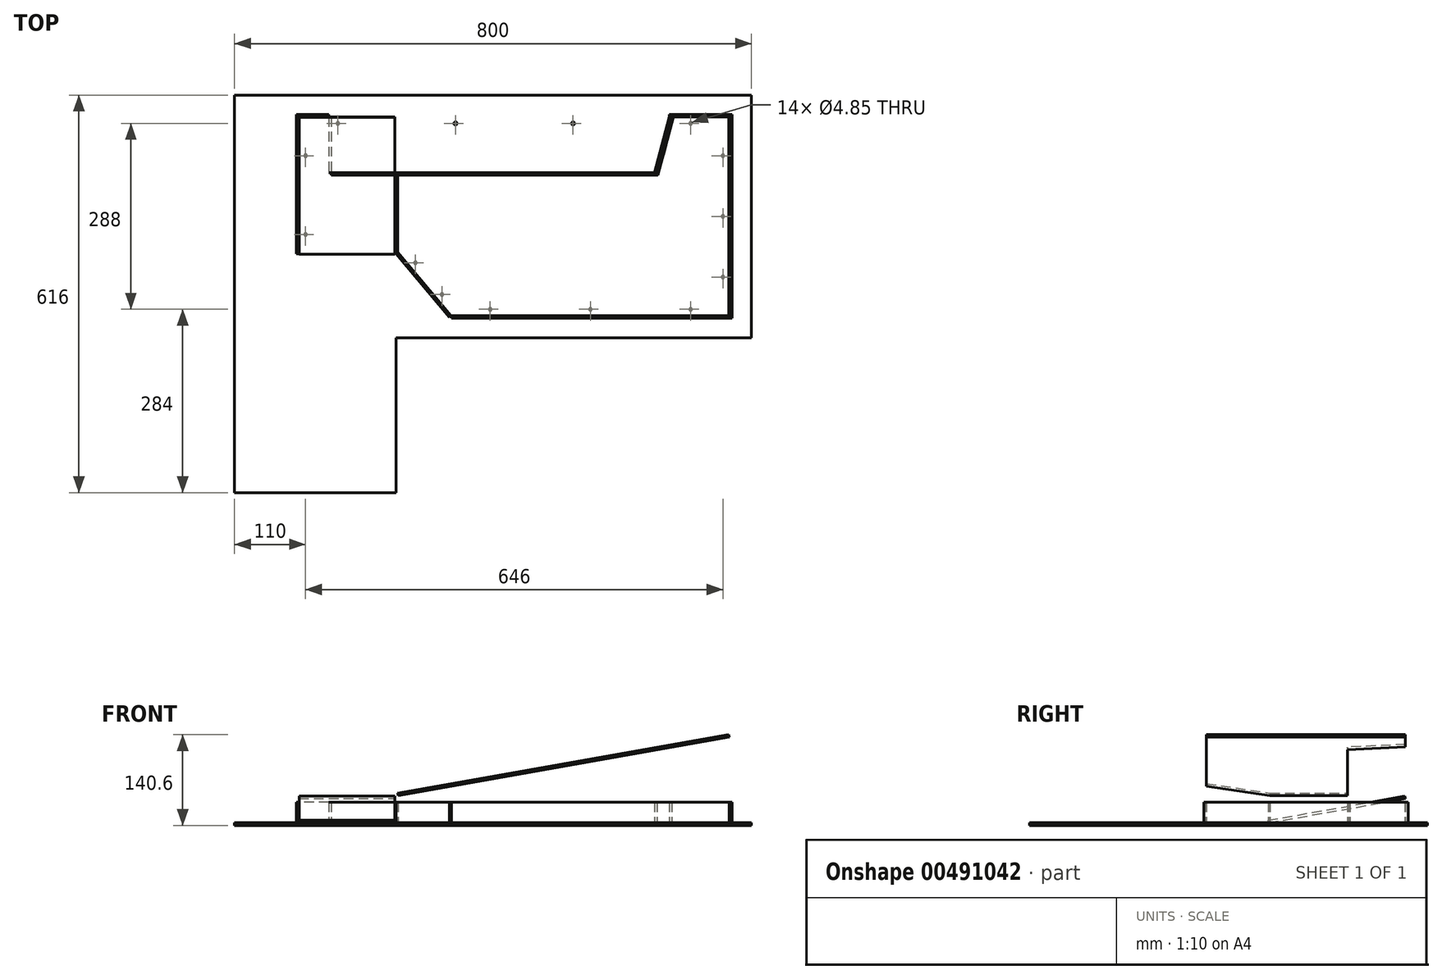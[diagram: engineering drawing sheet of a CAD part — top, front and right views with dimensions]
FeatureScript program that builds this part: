
annotation { "Feature Type Name" : "Feature", "Feature Type Description" : "" }
export const myFeature = defineFeature(function(context is Context, id is Id, definition is map)
    precondition{}
    {
        {
            assignVariable(context, id + "F0", {"name" : "altura", "anyValue" : 32});
        }
        {
            assignVariable(context, id + "F1", {"name" : "inclinacion", "anyValue" : 10});
        }
        {
            var Q0;
            Q0=qCreatedBy(makeId("Top.planeOp"),FACE);
            var sketch = newSketch(context, id + "F2", { "sketchPlane" : qUnion([Q0])});
            skLineSegment(sketch, "E0.bottom", {"start": v(0, 0) * mm, "end": v(250, 0) * mm});
            skLineSegment(sketch, "E0.top", {"start": v(0, 616) * mm, "end": v(800, 616) * mm});
            skLineSegment(sketch, "E0.left", {"start": v(0, 0) * mm, "end": v(0, 616) * mm});
            skLineSegment(sketch, "E0.right", {"start": v(800, 240) * mm, "end": v(800, 616) * mm});
            skLineSegment(sketch, "E1", {"start": v(250, 0) * mm, "end": v(250, 240) * mm});
            skLineSegment(sketch, "E2", {"start": v(250, 240) * mm, "end": v(800, 240) * mm});
            skLineSegment(sketch, "E3", {"start": v(0, 370) * mm, "end": v(250, 370) * mm, "construction": true});
            skLineSegment(sketch, "E4", {"start": v(250, 370) * mm, "end": v(250, 240) * mm, "construction": true});
            skLineSegment(sketch, "E5", {"start": v(787.3, 616) * mm, "end": v(787.3, 240) * mm, "construction": true});
            skLineSegment(sketch, "E6", {"start": v(800, 603.3) * mm, "end": v(0, 603.3) * mm, "construction": true});
            skLineSegment(sketch, "E7", {"start": v(12.7, 616) * mm, "end": v(12.7, 0) * mm, "construction": true});
            skSolve(sketch);
        }
        {
            var Q0;
            Q0=qSketchRegion(id+"F2",true);
            extrude(context, id + "F3", {"entities" : qUnion([Q0]), "depth" : 4 * mm});
        }
        {
            var Q0;
            Q0=makeQuery(id+"F3.opExtrude","CAP_FACE",FACE,{"disambiguationData":[OSD([sQuery(id+"F2.wireOp",EDGE,"E0.bottom"),sQuery(id+"F2.wireOp",EDGE,"E0.top"),sQuery(id+"F2.wireOp",EDGE,"E0.left"),sQuery(id+"F2.wireOp",EDGE,"E0.right"),sQuery(id+"F2.wireOp",EDGE,"E1"),sQuery(id+"F2.wireOp",EDGE,"E2")])],"isStart":false});
            var sketch = newSketch(context, id + "F4", { "sketchPlane" : qUnion([Q0])});
            skLineSegment(sketch, "E8.bottom", {"start": v(770, 270) * mm, "end": v(766, 270) * mm});
            skLineSegment(sketch, "E8.top", {"start": v(770, 586) * mm, "end": v(766, 586) * mm});
            skLineSegment(sketch, "E8.left", {"start": v(770, 270) * mm, "end": v(770, 586) * mm});
            skLineSegment(sketch, "E8.right", {"start": v(766, 270) * mm, "end": v(766, 586) * mm});
            skLineSegment(sketch, "E9.bottom", {"start": v(766, 586) * mm, "end": v(673.04, 586) * mm});
            skLineSegment(sketch, "E9.top", {"start": v(766, 582) * mm, "end": v(673.04, 582) * mm});
            skLineSegment(sketch, "E9.left", {"start": v(766, 586) * mm, "end": v(766, 582) * mm});
            skLineSegment(sketch, "E9.right", {"start": v(96, 586) * mm, "end": v(96, 582) * mm});
            skLineSegment(sketch, "E10.bottom", {"start": v(96, 582) * mm, "end": v(100, 582) * mm});
            skLineSegment(sketch, "E10.top", {"start": v(96, 370) * mm, "end": v(100, 370) * mm});
            skLineSegment(sketch, "E10.left", {"start": v(96, 582) * mm, "end": v(96, 370) * mm});
            skLineSegment(sketch, "E10.right", {"start": v(100, 582) * mm, "end": v(100, 370) * mm});
            skLineSegment(sketch, "E11.bottom", {"start": v(766, 270) * mm, "end": v(335.78, 270) * mm});
            skLineSegment(sketch, "E11.top", {"start": v(766, 274) * mm, "end": v(335.78, 274) * mm});
            skLineSegment(sketch, "E11.left", {"start": v(766, 270) * mm, "end": v(766, 274) * mm});
            skLineSegment(sketch, "E11.right", {"start": v(335.78, 270) * mm, "end": v(335.78, 274) * mm});
            skLineSegment(sketch, "E12", {"start": v(335.78, 274) * mm, "end": v(253.06, 372.57) * mm});
            skLineSegment(sketch, "E13", {"start": v(253.06, 372.57) * mm, "end": v(250, 370) * mm});
            skLineSegment(sketch, "E14", {"start": v(250, 370) * mm, "end": v(332.71, 271.43) * mm});
            skLineSegment(sketch, "E15", {"start": v(332.71, 271.43) * mm, "end": v(335.78, 274) * mm});
            skLineSegment(sketch, "E16", {"start": v(146, 586) * mm, "end": v(146, 582) * mm});
            skLineSegment(sketch, "E17", {"start": v(673.04, 586) * mm, "end": v(673.04, 582) * mm});
            skLineSegment(sketch, "E18.trimOffspring", {"start": v(146, 586) * mm, "end": v(96, 586) * mm});
            skLineSegment(sketch, "E19.trimOffspring", {"start": v(146, 582) * mm, "end": v(96, 582) * mm});
            skPoint(sketch, "E20", {"position": v(400, 616) * mm});
            skLineSegment(sketch, "E21.bottom", {"start": v(146, 582) * mm, "end": v(150, 582) * mm});
            skLineSegment(sketch, "E21.top", {"start": v(146, 496) * mm, "end": v(150, 496) * mm});
            skLineSegment(sketch, "E21.left", {"start": v(146, 582) * mm, "end": v(146, 496) * mm});
            skLineSegment(sketch, "E21.right", {"start": v(150, 582) * mm, "end": v(150, 496) * mm});
            skLineSegment(sketch, "E22.bottom", {"start": v(150, 496) * mm, "end": v(650, 496) * mm});
            skLineSegment(sketch, "E22.top", {"start": v(150, 492) * mm, "end": v(650, 492) * mm});
            skLineSegment(sketch, "E22.left", {"start": v(150, 496) * mm, "end": v(150, 492) * mm});
            skLineSegment(sketch, "E22.right", {"start": v(650, 496) * mm, "end": v(650, 492) * mm});
            skLineSegment(sketch, "E23", {"start": v(673.04, 582) * mm, "end": v(650, 496) * mm});
            skLineSegment(sketch, "E24", {"start": v(650, 496) * mm, "end": v(653.86, 494.96) * mm});
            skLineSegment(sketch, "E25", {"start": v(653.86, 494.96) * mm, "end": v(676.9, 580.96) * mm});
            skLineSegment(sketch, "E26", {"start": v(676.9, 580.96) * mm, "end": v(673.04, 582) * mm});
            skSolve(sketch);
        }
        {
            var Q0;
            Q0=makeQuery(id+"F4.imprint","IMPRINT",FACE,{"disambiguationData":[TD([[makeQuery(id+"F4.imprint","IMPRINT",EDGE,{"derivedFrom":sQuery(id+"F4.wireOp",EDGE,"E8.bottom")}),1.0]])]});
            var sketch = newSketch(context, id + "F5", { "sketchPlane" : qUnion([Q0])});
            skCircle(sketch, "E27", {"center": v(110, 400) * mm, "radius": 2.43 * mm});
            skCircle(sketch, "E28", {"center": v(110, 522) * mm, "radius": 2.43 * mm});
            skCircle(sketch, "E29", {"center": v(160, 572) * mm, "radius": 2.43 * mm});
            skCircle(sketch, "E30", {"center": v(706, 572) * mm, "radius": 2.43 * mm});
            skCircle(sketch, "E31", {"center": v(342, 572) * mm, "radius": 2.43 * mm});
            skCircle(sketch, "E32", {"center": v(524, 572) * mm, "radius": 2.43 * mm});
            skCircle(sketch, "E33", {"center": v(756, 334) * mm, "radius": 2.43 * mm});
            skCircle(sketch, "E34", {"center": v(395.78, 284) * mm, "radius": 2.43 * mm});
            skCircle(sketch, "E35", {"center": v(550.9, 284) * mm, "radius": 2.43 * mm});
            skCircle(sketch, "E36", {"center": v(756, 428) * mm, "radius": 2.43 * mm});
            skCircle(sketch, "E37", {"center": v(280, 356.02) * mm, "radius": 2.43 * mm});
            skCircle(sketch, "E38", {"center": v(321.15, 306.98) * mm, "radius": 2.43 * mm});
            skLineSegment(sketch, "E39", {"start": v(110, 370) * mm, "end": v(110, 582) * mm, "construction": true});
            skLineSegment(sketch, "E40", {"start": v(100, 572) * mm, "end": v(766, 572) * mm, "construction": true});
            skLineSegment(sketch, "E41", {"start": v(756, 582) * mm, "end": v(756, 274) * mm, "construction": true});
            skLineSegment(sketch, "E42", {"start": v(260.72, 379) * mm, "end": v(348.83, 274) * mm, "construction": true});
            skLineSegment(sketch, "E43", {"start": v(766, 284) * mm, "end": v(327.38, 284) * mm, "construction": true});
            skCircle(sketch, "E44", {"center": v(756, 522) * mm, "radius": 2.43 * mm});
            skCircle(sketch, "E45", {"center": v(706, 284) * mm, "radius": 2.43 * mm});
            skPoint(sketch, "E46", {"position": v(340.44, 284) * mm});
            skLineSegment(sketch, "E47", {"start": v(260.72, 379) * mm, "end": v(253.06, 372.57) * mm, "construction": true});
            skSolve(sketch);
        }
        {
            var Q0;
            Q0=makeQuery(id+"F4.imprint","IMPRINT",FACE,{"disambiguationData":[TD([[makeQuery(id+"F4.imprint","IMPRINT",EDGE,{"derivedFrom":sQuery(id+"F4.wireOp",EDGE,"E10.top")}),1.0]])]});
            extrude(context, id + "F6", {"entities" : qUnion([Q0]), "depth" : (getVariable(context, 'altura')) * mm});
        }
        {
            var Q0;
            {var subQ3=sQuery(id+"F4.wireOp",EDGE,"E9.right");Q0=makeQuery(id+"F4.imprint","IMPRINT",FACE,{"disambiguationData":[TD([[makeQuery(id+"F4.imprint","IMPRINT",EDGE,{"derivedFrom":subQ3}),1.0]])]});}
            var Q1;
            Q1=makeQuery(id+"F5.imprint","IMPRINT",FACE,{"disambiguationData":[TD([[makeQuery(id+"F5.imprint","IMPRINT",EDGE,{"derivedFrom":makeQuery(id+"F4.imprint","IMPRINT",EDGE,{"derivedFrom":sQuery(id+"F4.wireOp",EDGE,"E21.bottom")})}),-1.0]])]});
            var Q2;
            Q2=makeQuery(id+"F5.imprint","IMPRINT",FACE,{"disambiguationData":[TD([[makeQuery(id+"F5.imprint","IMPRINT",EDGE,{"derivedFrom":makeQuery(id+"F4.imprint","IMPRINT",EDGE,{"derivedFrom":sQuery(id+"F4.wireOp",EDGE,"E22.bottom")})}),-1.0]])]});
            var Q3;
            Q3=makeQuery(id+"F5.imprint","IMPRINT",FACE,{"disambiguationData":[TD([[makeQuery(id+"F5.imprint","IMPRINT",EDGE,{"derivedFrom":makeQuery(id+"F4.imprint","IMPRINT",EDGE,{"derivedFrom":sQuery(id+"F4.wireOp",EDGE,"E23")})}),1.0]])]});
            extrude(context, id + "F7", {"entities" : qUnion([Q0, Q1, Q2, Q3]), "depth" : (getVariable(context, 'altura')) * mm});
        }
        {
            var Q0;
            Q0=makeQuery(id+"F4.imprint","IMPRINT",FACE,{"disambiguationData":[TD([[makeQuery(id+"F4.imprint","IMPRINT",EDGE,{"derivedFrom":sQuery(id+"F4.wireOp",EDGE,"E9.bottom")}),1.0]])]});
            extrude(context, id + "F8", {"entities" : qUnion([Q0]), "depth" : (getVariable(context, 'altura')) * mm});
        }
        {
            var Q0;
            Q0=makeQuery(id+"F4.imprint","IMPRINT",FACE,{"disambiguationData":[TD([[makeQuery(id+"F4.imprint","IMPRINT",EDGE,{"derivedFrom":sQuery(id+"F4.wireOp",EDGE,"E8.bottom")}),-1.0]])]});
            extrude(context, id + "F9", {"entities" : qUnion([Q0]), "depth" : (getVariable(context, 'altura')) * mm});
        }
        {
            var Q0;
            Q0=makeQuery(id+"F4.imprint","IMPRINT",FACE,{"disambiguationData":[TD([[makeQuery(id+"F4.imprint","IMPRINT",EDGE,{"derivedFrom":sQuery(id+"F4.wireOp",EDGE,"E11.bottom")}),-1.0]])]});
            extrude(context, id + "F10", {"entities" : qUnion([Q0]), "depth" : (getVariable(context, 'altura')) * mm});
        }
        {
            var Q0;
            Q0=makeQuery(id+"F4.imprint","IMPRINT",FACE,{"disambiguationData":[TD([[makeQuery(id+"F4.imprint","IMPRINT",EDGE,{"derivedFrom":sQuery(id+"F4.wireOp",EDGE,"E12")}),1.0]])]});
            extrude(context, id + "F11", {"entities" : qUnion([Q0]), "depth" : (getVariable(context, 'altura')) * mm});
        }
        {
            var Q0;
            Q0=makeQuery(id+"F4.imprint","IMPRINT",FACE,{"disambiguationData":[TD([[makeQuery(id+"F4.imprint","IMPRINT",EDGE,{"derivedFrom":sQuery(id+"F4.wireOp",EDGE,"E8.bottom")}),1.0]])]});
            var sketch = newSketch(context, id + "F12", { "sketchPlane" : qUnion([Q0])});
            skLineSegment(sketch, "E48", {"start": v(250, 370) * mm, "end": v(0, 370) * mm, "construction": true});
            skSolve(sketch);
        }
        {
            var Q0;
            Q0=sQuery(id+"F12.wireOp",EDGE,"E48");
            cPlane(context, id + "F13", {"entities" : qUnion([Q0]), "cplaneType" : CPlaneType.LINE_ANGLE, "offset" : 25 * mm, "angle" : (90 - getVariable(context, 'inclinacion')) * degree, "width" : 150 * mm, "height" : 150 * mm});
        }
        {
            var Q0;
            Q0=qCreatedBy(id+"F13.planeOp",FACE);
            var sketch = newSketch(context, id + "F14", { "sketchPlane" : qUnion([Q0])});
            skLineSegment(sketch, "E49.bottom", {"start": v(100, 365.07) * mm, "end": v(248, 365.07) * mm});
            skLineSegment(sketch, "E49.top", {"start": v(100, 580.34) * mm, "end": v(248, 580.34) * mm});
            skLineSegment(sketch, "E49.left", {"start": v(100, 365.07) * mm, "end": v(100, 580.34) * mm});
            skLineSegment(sketch, "E49.right", {"start": v(248, 365.07) * mm, "end": v(248, 580.34) * mm});
            skSolve(sketch);
        }
        {
            var Q0;
            Q0=qSketchRegion(id+"F14",true);
            extrude(context, id + "F15", {"entities" : qUnion([Q0]), "depth" : 4 * mm});
        }
        {
            var Q0;
            Q0=makeQuery(id+"F15.opExtrude","SWEPT_FACE",FACE,{"disambiguationData":[OSD([sQuery(id+"F14.wireOp",EDGE,"E49.right")])]});
            var sketch = newSketch(context, id + "F16", { "sketchPlane" : qUnion([Q0])});
            skLineSegment(sketch, "E50", {"start": v(582, 45.32) * mm, "end": v(372.57, 45.32) * mm, "construction": true});
            skPoint(sketch, "E51", {"position": v(581.3, 45.32) * mm});
            skSolve(sketch);
        }
        {
            var Q0;
            Q0=sQuery(id+"F16.wireOp",EDGE,"E50");
            cPlane(context, id + "F17", {"entities" : qUnion([Q0]), "cplaneType" : CPlaneType.LINE_ANGLE, "offset" : 25 * mm, "angle" : (getVariable(context, 'inclinacion')) * degree, "width" : 150 * mm, "height" : 150 * mm});
        }
        {
            var Q0;
            Q0=qCreatedBy(id+"F17.planeOp",FACE);
            var sketch = newSketch(context, id + "F18", { "sketchPlane" : qUnion([Q0])});
            skLineSegment(sketch, "E52", {"start": v(778.1, -582) * mm, "end": v(778.1, -274) * mm});
            skLineSegment(sketch, "E53", {"start": v(778.1, -274) * mm, "end": v(341.23, -274) * mm});
            skLineSegment(sketch, "E54", {"start": v(341.23, -274) * mm, "end": v(257.24, -372.57) * mm});
            skLineSegment(sketch, "E55", {"start": v(257.24, -372.57) * mm, "end": v(257.24, -492) * mm});
            skLineSegment(sketch, "E56", {"start": v(257.24, -492) * mm, "end": v(666.53, -492) * mm});
            skLineSegment(sketch, "E57", {"start": v(666.53, -492) * mm, "end": v(666.53, -492) * mm});
            skLineSegment(sketch, "E58", {"start": v(691.02, -582) * mm, "end": v(778.1, -582) * mm});
            skLineSegment(sketch, "E59", {"start": v(691.02, -582) * mm, "end": v(666.53, -492) * mm});
            skLineSegment(sketch, "E60", {"start": v(663.42, -492) * mm, "end": v(687.9, -582) * mm, "construction": true});
            skSolve(sketch);
        }
        {
            var Q0;
            Q0=qSketchRegion(id+"F18",true);
            extrude(context, id + "F19", {"entities" : qUnion([Q0]), "oppositeDirection" : true, "depth" : 4 * mm});
        }
        {
            var Q0;
            Q0=qSketchRegion(id+"F5",true);
            extrude(context, id + "F20", {"entities" : qUnion([Q0]), "operationType" : NewBodyOperationType.REMOVE, "endBound" : BoundingType.THROUGH_ALL, "oppositeDirection" : true, "depth" : 25 * mm});
        }
    });
